# Revit family: IS_iLifeS_T4586_BIM_NL
name_source: partatom
category: Plumbing Fixtures
units: mm (PartAtom-declared; Revit-internal decimal feet)

## family parameters
Always vertical = No
Cut with Voids When Loaded = No
OmniClass Number = 23.45.05.14.14
OmniClass Title = Sinks/Lavatories
Part Type = Normal
Room Calculation Point = No
Round Connector Dimension = Use Diameter
Shared = No
Work Plane-Based = No

## types (2) — shared parameters
Accessories = https://www.idealstandard.nl
Afmetingen = 450 x 250 x 140 mm
AfstandsEenheid = Millimeter
AreaUnits = millimetres
AssetType = Fixed
Auteur = Ideal Standard
BIMObjectName = IS_IdealStandard_Wall-hung washbasins_i.lifeS_T4586
BIMobject category = Wash Basins
BIMobject category code = wash-basins
BIMobject main category = Sanitary
BIMobject main category code = sanitary
Beschrijvinggarantie = Herstellergarantie
BimObjectNaam = IS_IdealStandard_Wall-hung washbasins_i.lifeS_T4586
Brand = Ideal Standard
Brand url = https://www.idealstandard.nl
Breedte = 449.575541
Category = Sanitary
ConnectionType = Plumbing
CurrencyUnit = €
CurrentRevision = 1
Date of publishing = 27/05/2022
Diepte = 249 mm
DurationUnit = Years
DuurEenheid = Jahre
Edition number = 1
ElementType = Fixed
ExpectedLife = 99
Garantieunits = Jahre
Help = https://www.idealstandard.nl
Hoogte = 140.004396650985
Hulp = https://www.idealstandard.nl
IFC Classification = Sanitary Terminal
IfcExportAs = IfcSanitaryTerminalType
IfcExportType = TOILETPAN
Installatieinstructies = https://www.idealstandard.nl
Installation instructions = https://www.idealstandard.nl
InstallationInstructions = https://www.idealstandard.nl
Lengte = 249 mm
LinearUnits = Millimetres
MaintenanceInformation = https://www.idealstandard.nl
Manufacturer = Ideal Standard
Manufacturer name = Ideal Standard
ManufacturerURL = https://www.idealstandard.nl
Materiaal = Feiner Schamotte
Material = Finefireclay
Material main = Finefireclay
Merk = Ideal Standard
ModelReference = i.life S  handrinse washbasin 45 cm
NBS Reference Code = 45-35-70/369
NBS Reference Description = Wall hung wash basins
Name = Wall-hung washbasins_i.lifeS_T4586_IdealStandard
NettWeight = 6.7
Nettogewicht = 6.7
NominalDepth = 249 mm
NominalHeight = 140 mm
NominalLength = 249 mm
NominalWidth = 450 mm
Normen = Wall-hung washbasins_i.lifeS_T4586_IdealStandard
OmniClass Code = 23-11 21 21 13
OmniClass Description = Catch Basin
Ophangingwastafel = Wand aufgehängt
OppervlakteEenheid = Millimeter
PredefinedType = Sanitary
Product Guid = 5dfd4467-300a-4763-8289-e12a17931d5b
Product SKU = T4586
Product certification = https://www.idealstandard.nl
Product data url = https://bimobject.com
Product family = I.life S
Product group = Saniatry: Basins
Product name = i.life S  handrinse washbasin 45 cm
Product url = https://www.idealstandard.nl
ProductInformation = https://www.idealstandard.nl
Productinformatie = https://www.idealstandard.nl
QR code = http://bimobject.com
Referentie = i.life S  handrinse washbasin 45 cm
ReplacementCost = 0
Revisie = 1
Shape = Sculpture
Size = 450 x 250 x 140 mm
Space = Internal
SpareParts = https://www.idealstandard.nl
Technical description = https://www.idealstandard.nl
Telefoonnummer = 077 355 08 08
Typeconnectie = Installation
Typewastafel = Handwaschbecken
UNSPSC Code = 301815
URL = https://www.idealstandard.nl
Uniclass 2015 Code = Pr_40_20_96_96
Uniclass 2015 Name = Wall-hung washbasins
Uniclass2015Beschrijving = Wall-hung washbasins
Uniclass2015Code = Pr_40_20_96_96
Uniclass2015Referentie = Pr_40_20_96_96
Uniclass2015Title = Wall-hung washbasins
Uniclass2015Version = v.25
Urlproducent = https://www.idealstandard.nl
ValutaEenheid = Euro
Versie = 1
Version = 1
VolumeUnits = Litres
Volumeunits = Liter
Vorm = geformt
WRASURL = https://www.wrasapprovals.co.uk
WarrantyDescription = manufacturer warranty
WarrantyDurationUnit = years
WashHandBasinMounting = Wall hung Basin
WashHandBasinType = Wall hung Basin
Wisselstukken = https://www.idealstandard.nl
Youtube clip = https://www.youtube.com
zero-valued in all types: BrutoGewicht, Cost, Vervangingskosten

## per-type parameters (varying)
| type | Afwerking | Artikelnummer | Artikelomschrijving | BarCode | Color | Description | Eigenschappen | Features | Finish | GTIN code | Kleur | MainColor | Model | ModelNumber |
| T458601 - i.life S  handrinse washbasin 45 cm - White | Weiß | T458601 | Ideal Standard i.life S Handbrause 45 cm mit Hahnloch rechts, mit Überlauf, weiß im Karton, EU-Palette | 8014140491620 | Weiß | Ideal Standard i.life S  handrinse 45 cm with right hand taphole, with overflow, white in carton box, EU pallet | Handbrause 45 cm mit Hahnloch rechts, mit Überlauf, weiß im Karton, EU-Palette | handrinse 45 cm with right hand taphole, with overflow, white in carton box, EU pallet | White | https://8014140491620 | Weiß | White | T458601 | T458601 |
| T4586MA - i.life S  handrinse washbasin 45 cm - Ideal Plus White | Ideales Plus-Weiß | T4586MA | Ideal Standard i.life S Handbrause 45 cm mit Hahnloch rechts, mit Überlauf, weiß Ideal Plus, im Karton, EU-Palette | 8014140491637 | Ideales Plus-Weiß | Ideal Standard i.life S  handrinse 45 cm with right hand taphole, with overflow, white Ideal Plus, in carton box, EU pallet | Handbrause 45 cm mit Hahnloch rechts, mit Überlauf, weiß Ideal Plus, im Karton, EU-Palette | handrinse 45 cm with right hand taphole, with overflow, white Ideal Plus, in carton box, EU pallet | Ideal Plus White | https://8014140491637 | Ideales Plus-Weiß | Ideal Plus White | T4586MA | T4586MA |

## geometry (parser evidence)
native form markers: Sweep x3
no freeform markers — native parametric forms only
